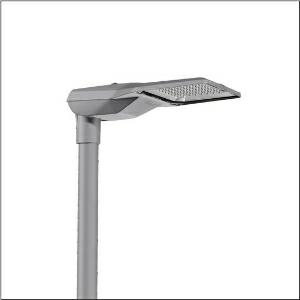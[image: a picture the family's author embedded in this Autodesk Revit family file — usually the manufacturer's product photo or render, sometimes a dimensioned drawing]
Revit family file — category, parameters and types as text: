
# Revit family: streetlight_sl_21_midi___pc-l_5xe3f43s08mb_b5db
name_source: partatom
category: Lighting Fixtures
units: mm (PartAtom-declared; Revit-internal decimal feet)

## family parameters
Cut with Voids When Loaded = No
Host = Face
Light Source = No
Part Type = Normal
Room Calculation Point = No
Round Connector Dimension = Use Diameter
Shared = No

## types (1)
- --- (1 x LED, 19200 lm, 147 W, 4000K)
    Apparent Load = 147 VA
    CIE Flux Codes = 38 78 98 100 100
    Color Rendering = 70
    Color Temperature = 4000K
    Default Elevation = 1800 mm
    Description = Streetlight SL 21 midi, mast luminaire, primary light control with lens, of PMMA, primary optical cover: cover, of toughened safety glass, transparent, light distribution: PC-L, light emission: direct distribution, primary light characteristic: asymmetric, left, installation type: side-entry, post-top, LED, High Power LED, rated luminous flux: 19.200lm, luminous efficacy: 131lm/W, light colour: 740, colour temperature: 4000K, control gear: D4i, control: overheat protection, constant luminous flux control, time-dependent luminous flux control, flexible luminous flux parameterisation, pre-setting: logarithmic dimming characteristic, mains connection: 230..240V, AC, 50/60Hz, start of lifetime: 147W, end of service life: 155W, reduction: 65W, luminaire housing, of diecast aluminium, powder-coated, SITECO metallic grey (DB 702S), corrosivity category C5 high according to DIN EN ISO 12944, please order mast flange separately, inclination adjustable: 0°, 5°, 10°, 15°, sealing non-destructively replaceable, multi-level sealing system, length: 644mm, width: 335mm, height: 110mm, mast flange for spigot size: 42mm (side-entry): 5XC10008XM4, 60/48mm (side-entry/post-top): 5XC10108XM2, 76/60mm (side-entry/post-top): 5XC10108XM1, mounting height: 4..8m, Smart Interface above, protection rating (complete): IP66, insulation class (complete): insulation class II (safety insulation), certification: CE, ENEC, ENEC+, VDE, impact resistance: IK10, permissible operating ambient temperature for outdoor applications: -40..+50°C, standard-compliant lighting for roads and squares, packaging unit: 1 piece

Light Distribution: PC-L
    Height = 111 mm
    Lamp = 1 x LED
    Lamp Light Flux = 19200 lm
    Lamp Power = 147 W
    Lamp count = 1
    Length = 644 mm
    Luminous efficacy = 131 lm/W
    Manufacturer = Siteco
    ModVariant = No
    Model = 5XE3F43S08MB
    Number of Poles = 1
    OnlyDefault = Yes
    Power Factor = 1
    Product Name = Streetlight SL 21 midi | PC-L
    Product group = mast luminaire | pylon top
    ProductGroupID = 6100
    Protection Class = Protection class II
    Protection Degree = IP 66
    RLX_Detail_Level = 1
    RLX_Emergency_Light_Flux = 0 lm
    RLX_Emergency_Type = 0
    RLX_Emergency_Type_DB = No
    RlxData = <blob elided: 29493 chars, md5=a056cffd>
    Socket = socket
    Standby Power = 0 W
    System Light Flux = 19200 lm
    System Power = 147 W
    Type Comments = factory setting: luminous flux: 100 % | dim-lin: 254 | 750 mA
    Type Image = l_1004302.jpg
    URL = http://relux.com
    VarID = @adj_072003
    Voltage = 0 V
    Weight = 0.00 kg
    Width = 336 mm

## geometry (parser evidence)
native form markers: Blend x4, Sweep x11
no freeform markers — native parametric forms only
